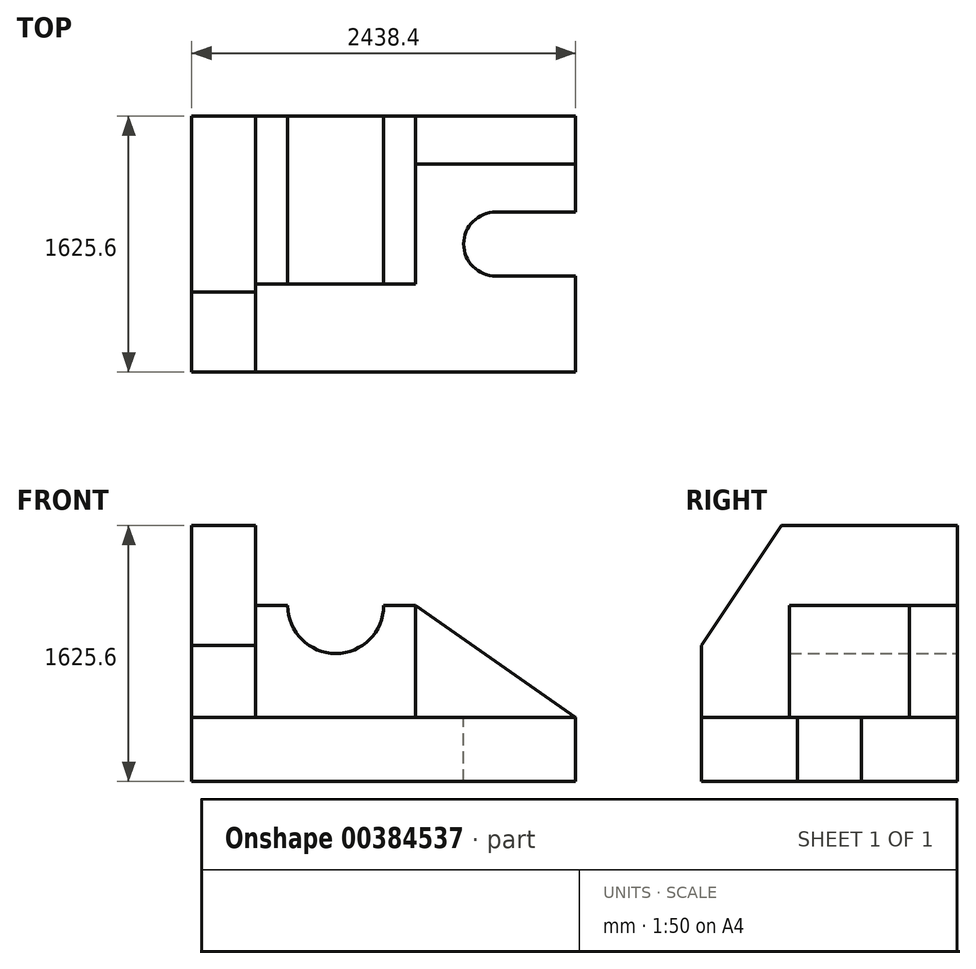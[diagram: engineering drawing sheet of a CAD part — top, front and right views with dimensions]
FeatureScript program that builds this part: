
annotation { "Feature Type Name" : "Feature", "Feature Type Description" : "" }
export const myFeature = defineFeature(function(context is Context, id is Id, definition is map)
    precondition{}
    {
        {
            var Q0;
            Q0=qCreatedBy(makeId("Front.planeOp"),FACE);
            var sketch = newSketch(context, id + "F0", { "sketchPlane" : qUnion([Q0])});
            skLineSegment(sketch, "E0", {"start": v(0, 0) * mm, "end": v(2438.4, 0) * mm});
            skLineSegment(sketch, "E1", {"start": v(2438.4, 0) * mm, "end": v(2438.4, 406.4) * mm});
            skLineSegment(sketch, "E2", {"start": v(2438.4, 406.4) * mm, "end": v(0, 406.4) * mm});
            skLineSegment(sketch, "E3", {"start": v(0, 406.4) * mm, "end": v(0, 0) * mm});
            skSolve(sketch);
        }
        {
            var Q0;
            Q0 = qSketchRegion(id + "F0", true);
            extrude(context, id + "F1", {"entities" : qUnion([Q0]), "oppositeDirection" : true, "depth" : 1625.6 * mm});
        }
        {
            var Q0;
            Q0=makeQuery(id+"F1.opExtrude","CAP_FACE",FACE,{"disambiguationData":[OSD([sQuery(id+"F0.wireOp",EDGE,"E0"),sQuery(id+"F0.wireOp",EDGE,"E1"),sQuery(id+"F0.wireOp",EDGE,"E2"),sQuery(id+"F0.wireOp",EDGE,"E3")])],"isStart":false});
            var sketch = newSketch(context, id + "F2", { "sketchPlane" : qUnion([Q0])});
            skLineSegment(sketch, "E4", {"start": v(-2438.4, 406.4) * mm, "end": v(-1422.4, 1117.6) * mm});
            skLineSegment(sketch, "E5", {"start": v(-1422.4, 1117.6) * mm, "end": v(-1422.4, 406.4) * mm});
            skSolve(sketch);
        }
        {
            var Q0;
            {var subQ0=sQuery(id+"F2.wireOp",EDGE,"E4");Q0=makeQuery(id+"F2.imprint","IMPRINT",FACE,{"disambiguationData":[TD([[makeQuery(id+"F2.imprint","IMPRINT",EDGE,{"derivedFrom":subQ0}),-1.0]])]});}
            extrude(context, id + "F3", {"entities" : qUnion([Q0]), "oppositeDirection" : true, "depth" : 304.8 * mm});
        }
        {
            var Q0;
            Q0=makeQuery(id+"F1.opExtrude","SWEPT_FACE",FACE,{"disambiguationData":[OSD([sQuery(id+"F0.wireOp",EDGE,"E2")])]});
            var sketch = newSketch(context, id + "F4", { "sketchPlane" : qUnion([Q0])});
            skLineSegment(sketch, "E6", {"start": v(2438.4, 0) * mm, "end": v(2438.4, 609.6) * mm});
            skLineSegment(sketch, "E7", {"start": v(2438.4, 609.6) * mm, "end": v(1930.4, 609.6) * mm});
            skArc(sketch, "E8", {"start": v(1930.4, 1016) * mm, "mid": v(1727.2, 812.8) * mm, "end": v(1930.4, 609.6) * mm});
            skLineSegment(sketch, "E9", {"start": v(2438.4, 1016) * mm, "end": v(1930.4, 1016) * mm});
            skSolve(sketch);
        }
        {
            var Q0;
            Q0 = qSketchRegion(id + "F4", true);
            var Q1;
            {var subQ0=sQuery(id+"F4.wireOp",EDGE,"E7");Q1=makeQuery(id+"F4.imprint","IMPRINT",FACE,{"disambiguationData":[TD([[makeQuery(id+"F4.imprint","IMPRINT",EDGE,{"derivedFrom":subQ0}),-1.0]])]});}
            extrude(context, id + "F5", {"entities" : qUnion([Q0, Q1]), "operationType" : NewBodyOperationType.REMOVE, "oppositeDirection" : true, "depth" : 406.4 * mm});
        }
        {
            var Q0;
            Q0=makeQuery(id+"F1.opExtrude","SWEPT_FACE",FACE,{"disambiguationData":[OSD([sQuery(id+"F0.wireOp",EDGE,"E3")])]});
            var sketch = newSketch(context, id + "F6", { "sketchPlane" : qUnion([Q0])});
            skLineSegment(sketch, "E10", {"start": v(-1625.6, 406.4) * mm, "end": v(-1625.6, 1625.6) * mm});
            skLineSegment(sketch, "E11", {"start": v(0, 406.4) * mm, "end": v(-1625.6, 406.4) * mm});
            skLineSegment(sketch, "E12", {"start": v(-1625.6, 1625.6) * mm, "end": v(-508, 1625.6) * mm});
            skLineSegment(sketch, "E13", {"start": v(-508, 1625.6) * mm, "end": v(0, 863.6) * mm});
            skLineSegment(sketch, "E14", {"start": v(0, 863.6) * mm, "end": v(0, 406.4) * mm});
            skSolve(sketch);
        }
        {
            var Q0;
            Q0=makeQuery(id+"F1.opExtrude","CAP_FACE",FACE,{"disambiguationData":[OSD([sQuery(id+"F0.wireOp",EDGE,"E0"),sQuery(id+"F0.wireOp",EDGE,"E1"),sQuery(id+"F0.wireOp",EDGE,"E2"),sQuery(id+"F0.wireOp",EDGE,"E3")])],"isStart":false});
            var sketch = newSketch(context, id + "F7", { "sketchPlane" : qUnion([Q0])});
            skLineSegment(sketch, "E15", {"start": v(-1422.4, 406.4) * mm, "end": v(-1422.4, 1117.6) * mm});
            skLineSegment(sketch, "E16", {"start": v(-1422.4, 1117.6) * mm, "end": v(-1219.2, 1117.6) * mm});
            skLineSegment(sketch, "E17", {"start": v(-406.4, 1117.6) * mm, "end": v(-406.4, 406.4) * mm});
            skLineSegment(sketch, "E18", {"start": v(-406.4, 406.4) * mm, "end": v(-1422.4, 406.4) * mm});
            skArc(sketch, "E19", {"start": v(-1219.2, 1117.6) * mm, "mid": v(-914.4, 812.8) * mm, "end": v(-609.6, 1117.6) * mm});
            skLineSegment(sketch, "E20.trimOffspring", {"start": v(-609.6, 1117.6) * mm, "end": v(-406.4, 1117.6) * mm});
            skSolve(sketch);
        }
        {
            var Q0;
            Q0=makeQuery(id+"F7.imprint","IMPRINT",FACE,{"disambiguationData":[TD([[makeQuery(id+"F7.imprint","IMPRINT",EDGE,{"derivedFrom":sQuery(id+"F7.wireOp",EDGE,"E15")}),-1.0]])]});
            extrude(context, id + "F8", {"entities" : qUnion([Q0]), "operationType" : NewBodyOperationType.ADD, "oppositeDirection" : true, "depth" : 1066.8 * mm});
        }
        {
            var Q0;
            Q0=makeQuery(id+"F6.imprint","IMPRINT",FACE,{"disambiguationData":[TD([[makeQuery(id+"F6.imprint","IMPRINT",EDGE,{"derivedFrom":sQuery(id+"F6.wireOp",EDGE,"E10")}),-1.0]])]});
            extrude(context, id + "F9", {"entities" : qUnion([Q0]), "oppositeDirection" : true, "depth" : 406.4 * mm});
        }
    });
